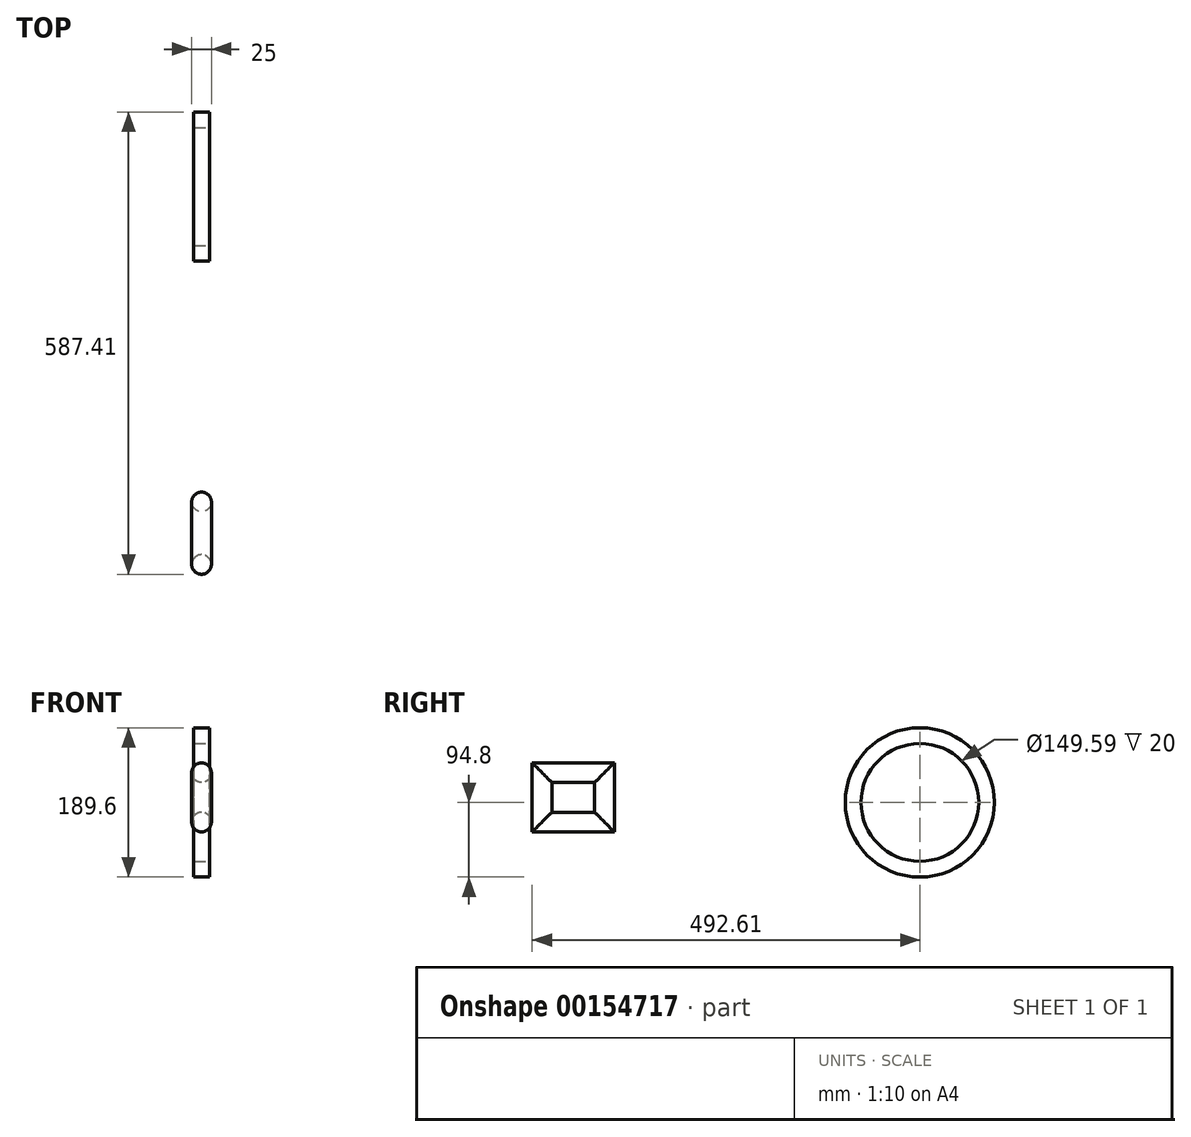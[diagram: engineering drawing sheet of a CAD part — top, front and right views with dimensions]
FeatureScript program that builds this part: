
annotation { "Feature Type Name" : "Feature", "Feature Type Description" : "" }
export const myFeature = defineFeature(function(context is Context, id is Id, definition is map)
    precondition{}
    {
        {
            var Q0;
            Q0=qCreatedBy(makeId("Top.planeOp"),FACE);
            var sketch = newSketch(context, id + "F0", { "sketchPlane" : qUnion([Q0])});
            skPoint(sketch, "E0.middle", {"position": v(0, 0) * mm});
            skFitSpline(sketch, "E1", {"points": [v(-25.85, 47.45) * mm, v(-49.11, 16.43) * mm, v(-46.53, -31.57) * mm, v(-9.6, -54.83) * mm, v(38.03, -44.5) * mm, v(50.96, -6.1) * mm, v(49.11, 33.79) * mm, v(28.43, 47.82) * mm], "startDerivative": vector(-198.38, -191.89) * mm, "endDerivative": vector(-221.49, 89.28) * mm});
            skSolve(sketch);
        }
        {
            var Q0;
            Q0=sQuery(id+"F0.wireOp",VERTEX,"E1.7.internal");
            var Q1;
            Q1=sQuery(id+"F0.wireOp",EDGE,"E1");
            cPlane(context, id + "F1", {"entities" : qUnion([Q0, Q1]), "cplaneType" : CPlaneType.CURVE_POINT, "offset" : 25 * mm, "width" : 150 * mm, "height" : 150 * mm});
        }
        {
            var Q0;
            Q0=qCreatedBy(id+"F1.planeOp",FACE);
            var sketch = newSketch(context, id + "F2", { "sketchPlane" : qUnion([Q0])});
            skCircle(sketch, "E2", {"center": v(-54.98, 0) * mm, "radius": 10 * mm});
            skSolve(sketch);
        }
        {
            var Q0;
            Q0=makeQuery(id+"FM90p60orfqvniN_0.imprint","IMPRINT",FACE,{"disambiguationData":[TD([[makeQuery(id+"FM90p60orfqvniN_0.imprint","IMPRINT",EDGE,{"derivedFrom":sQuery(id+"FM90p60orfqvniN_0.wireOp",EDGE,"jZGmsH9N-qo8T-pZnr-7KSp-CK4SuP5fSOtZ")}),1.0]])]});
            var Q1;
            Q1=sQuery(id+"F2.wireOp",EDGE,"E2");
            var Q2;
            Q2=sQuery(id+"F0.wireOp",EDGE,"E1");
            sweep(context, id + "F3", {"bodyType" : ToolBodyType.SURFACE, "profiles" : qUnion([Q0]), "surfaceProfiles" : qUnion([Q1]), "path" : qUnion([Q2])});
        }
        {
            var Q0;
            Q0=qCreatedBy(makeId("Right.planeOp"),FACE);
            var sketch = newSketch(context, id + "F4", { "sketchPlane" : qUnion([Q0])});
            skLineSegment(sketch, "E3.bottom", {"start": v(-237.08, 37.85) * mm, "end": v(-157.57, 37.85) * mm});
            skLineSegment(sketch, "E3.top", {"start": v(-237.08, -25) * mm, "end": v(-157.57, -25) * mm});
            skLineSegment(sketch, "E3.left", {"start": v(-237.08, 37.85) * mm, "end": v(-237.08, -25) * mm});
            skLineSegment(sketch, "E3.right", {"start": v(-157.57, 37.85) * mm, "end": v(-157.57, -25) * mm});
            skSolve(sketch);
        }
        {
            var Q0;
            Q0=qCreatedBy(makeId("Top.planeOp"),FACE);
            var sketch = newSketch(context, id + "F5", { "sketchPlane" : qUnion([Q0])});
            skCircle(sketch, "E4", {"center": v(0, -237.08) * mm, "radius": 12.5 * mm});
            skSolve(sketch);
        }
        {
            var Q0;
            Q0=makeQuery(id+"F5.imprint","IMPRINT",FACE,{"disambiguationData":[TD([[makeQuery(id+"F5.imprint","IMPRINT",EDGE,{"derivedFrom":sQuery(id+"F5.wireOp",EDGE,"E4")}),1.0]])]});
            var Q1;
            Q1=sQuery(id+"F4.wireOp",EDGE,"E3.left");
            var Q2;
            Q2=sQuery(id+"F4.wireOp",EDGE,"E3.top");
            var Q3;
            Q3=sQuery(id+"F4.wireOp",EDGE,"E3.bottom");
            var Q4;
            Q4=sQuery(id+"F4.wireOp",EDGE,"E3.right");
            sweep(context, id + "F6", {"profiles" : qUnion([Q0]), "path" : qUnion([Q1, Q2, Q3, Q4])});
        }
        {
            var Q0;
            Q0=qCreatedBy(makeId("Right.planeOp"),FACE);
            var sketch = newSketch(context, id + "F7", { "sketchPlane" : qUnion([Q0])});
            skCircle(sketch, "E5", {"center": v(243.03, 0) * mm, "radius": 50 * mm});
            skSolve(sketch);
        }
        {
            var Q0;
            Q0=qCreatedBy(makeId("Top.planeOp"),FACE);
            var sketch = newSketch(context, id + "F8", { "sketchPlane" : qUnion([Q0])});
            skLineSegment(sketch, "E6.bottom", {"start": v(10, 168.23) * mm, "end": v(-10, 168.23) * mm});
            skLineSegment(sketch, "E6.top", {"start": v(10, 148.23) * mm, "end": v(-10, 148.23) * mm});
            skLineSegment(sketch, "E6.left", {"start": v(10, 168.23) * mm, "end": v(10, 148.23) * mm});
            skLineSegment(sketch, "E6.right", {"start": v(-10, 168.23) * mm, "end": v(-10, 148.23) * mm});
            skPoint(sketch, "E6.middle", {"position": v(0, 158.23) * mm});
            skSolve(sketch);
        }
        {
            var Q0;
            Q0=makeQuery(id+"F8.imprint","IMPRINT",FACE,{"disambiguationData":[TD([[makeQuery(id+"F8.imprint","IMPRINT",EDGE,{"derivedFrom":sQuery(id+"F8.wireOp",EDGE,"E6.bottom")}),1.0]])]});
            var Q1;
            Q1=sQuery(id+"F7.wireOp",EDGE,"E5");
            sweep(context, id + "F9", {"profiles" : qUnion([Q0]), "path" : qUnion([Q1])});
        }
    });
